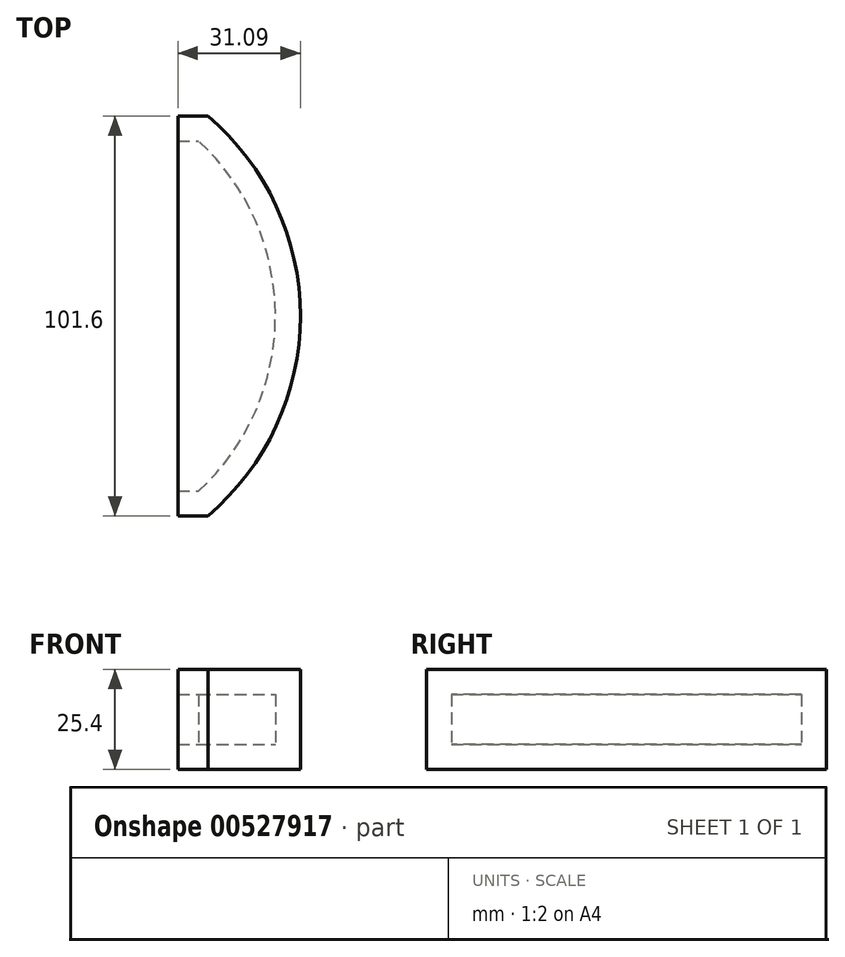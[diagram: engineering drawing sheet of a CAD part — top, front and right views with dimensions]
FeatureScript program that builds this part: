
annotation { "Feature Type Name" : "Feature", "Feature Type Description" : "" }
export const myFeature = defineFeature(function(context is Context, id is Id, definition is map)
    precondition{}
    {
        {
            var Q0;
            Q0=qCreatedBy(makeId("Top.planeOp"),FACE);
            var sketch = newSketch(context, id + "F0", { "sketchPlane" : qUnion([Q0])});
            skLineSegment(sketch, "E0.bottom", {"start": v(-62.42, 85.42) * mm, "end": v(-54.8, 85.42) * mm});
            skLineSegment(sketch, "E0.top", {"start": v(-62.42, -16.18) * mm, "end": v(-54.8, -16.18) * mm});
            skLineSegment(sketch, "E0.left", {"start": v(-62.42, 85.42) * mm, "end": v(-62.42, -16.18) * mm});
            skLineSegment(sketch, "E0.right", {"start": v(-54.8, 85.42) * mm, "end": v(-54.8, -16.18) * mm});
            skArc(sketch, "E1", {"start": v(-54.8, -16.18) * mm, "mid": v(-31.33, 34.62) * mm, "end": v(-54.8, 85.42) * mm});
            skSolve(sketch);
        }
        {
            var Q0;
            Q0=makeQuery(id+"F0.imprint","IMPRINT",FACE,{"disambiguationData":[TD([[makeQuery(id+"F0.imprint","IMPRINT",EDGE,{"derivedFrom":sQuery(id+"F0.wireOp",EDGE,"E0.bottom")}),-1.0]])]});
            var Q1;
            Q1=makeQuery(id+"F0.imprint","IMPRINT",FACE,{"disambiguationData":[TD([[makeQuery(id+"F0.imprint","IMPRINT",EDGE,{"derivedFrom":sQuery(id+"F0.wireOp",EDGE,"E0.right")}),1.0]])]});
            extrude(context, id + "F1", {"entities" : qUnion([Q0, Q1]), "depth" : 25.4 * mm, "offsetDistance" : 25.4 * mm});
        }
        {
            var Q0;
            Q0=makeQuery(id+"F1.opExtrude","SWEPT_FACE",FACE,{"disambiguationData":[OSD([sQuery(id+"F0.wireOp",EDGE,"E0.left")])]});
            shell(context, id + "F2", {"entities" : qUnion([Q0]), "thickness" : 6.35 * mm});
        }
    });
